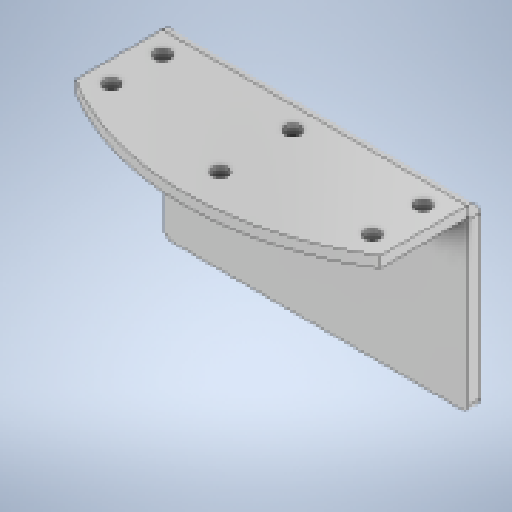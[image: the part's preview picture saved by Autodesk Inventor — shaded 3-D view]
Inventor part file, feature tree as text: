
AUTODESK INVENTOR PART (.ipt)
format: ipt  version: 2024.2 (Build 282272000, 272)  size: 223,232 bytes
history: native  units: in
note: dims shown in document units (in); Inventor stores cm internally (conversion verified against a paired STEP export)
features: other x8, reference x8, sketch x6, sheet_metal_op x4, hole x2, chamfer x1
ambient origin geometry x8: Origin, YZ Plane, XZ Plane, XY Plane, X Axis, Y Axis, Z Axis, Center Point
bodies: Solid1 (feature_tree)
feature tree (29):
  sheet_metal_op  "Face1"
  sheet_metal_op  "Flange1"
  chamfer  "Corner Round1"
  hole  "Hole2"  [1 undecoded]
  hole  "Hole3"  [1 undecoded]
  sketch  "Sketch1"  dims[d0=1.6575in d1=0.9843in]
  other  "Plate1"
  sketch  "Sketch4"  dims[d2=0.0591in d13=0.0591in]
  other  "Plate2"
  sheet_metal_op  "Bend1"
  sheet_metal_op  "Corner1"
  sketch  "Sketch5"  dims[d14=0.0295in]
  reference  "Reference8"
  sketch  "Sketch6"  dims[d15=0.1181in]
  sketch  "Sketch7"  dims[d16=0.0122in]
  reference  "Reference9"
  reference  "Reference10"
  reference  "Reference11"
  reference  "Reference12"
  reference  "Reference13"
  reference  "Reference14"
  sketch  "Sketch8"  dims[d17=0.9843in d18=90.0deg d19=0.0122in d20=0.2362in d21=0.0591in d22=0.0122in d23=0.5118in d24=0.0591in d25=0.0in d26=0.0394in d27=0.3937in d28=0.1181in d29=0.7087in d30=0.2756in d31=0.0827in d32=0.2362in d33=0.1575in d34=0.0787in d35=90.0deg d36=0.315in d37=0.8108in d38=0.0827in d39=0.1181in d40=0.1575in d41=0.0787in d42=90.0deg d43=0.0591in d44=0.0in d45=0.5197in d46=0.0591in d47=0.0in]
  reference  "Reference15"
  other  "Cut1"
  other  "Cut2"
  other  "2_Arm.iam"
  other  "axis_2_bottom_frame:1"
  other  "HTD-45H:2"
  other  "HTD-45H:1"
note: 2 required parameter values undecoded (feature->parameter linkage not recoverable at this tier; creation-order binding heuristic only, values carry confidence <= 0.55)
